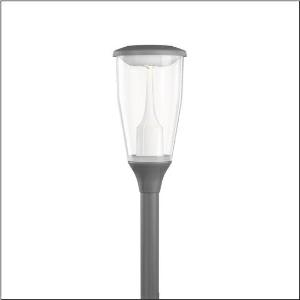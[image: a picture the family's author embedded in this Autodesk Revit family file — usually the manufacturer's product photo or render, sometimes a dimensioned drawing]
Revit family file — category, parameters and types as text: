
# Revit family: dl_11_iq___p1_0a_5xa5565bf14h000022_0962
name_source: partatom
category: Lighting Fixtures
units: mm (PartAtom-declared; Revit-internal decimal feet)

## family parameters
Cut with Voids When Loaded = No
Host = Face
Light Source = No
Part Type = Normal
Room Calculation Point = No
Round Connector Dimension = Use Diameter
Shared = No

## types (1)
- --- (1 x LED, 1530 lm, 12.9 W, 2200K)
    Apparent Load = 13 VA
    CIE Flux Codes = 34 63 91 95 100
    Color Rendering = 70
    Color Temperature = 2200K
    Default Elevation = 1800 mm
    Description = DL 11 iQ, mast luminaire, Module 540 iQ-SR, primary light control with 3 zone facetted reflector, of plastic, silver coated, highly specular, structured, primary optical cover: cover, of PMMA, transparent, light distribution: P1.0a, light emission: direct distribution, primary light characteristic: asymmetric, installation type: post-top, LED, High Power LED, rated luminous flux: 1.560lm, luminous efficacy: 149lm/W, light colour: 722, colour temperature: 2200K, control: Street-Remote, Auto-Match, Temp-Guard, Lumen-Switch, Night-Set, Smart-Wire, Light-Fading, Desk-Remote (wireless, voltage-free reading and setting of iQ features in the workshop via application-optimized NFC function/RFID function), optimised constant luminous flux control (CLO 2.0), mains connection: 220..240V, AC, 50/60Hz, connection cable pre-assembled, cable length: 5,5m, start of lifetime: 13W, end of service life: 13W, reduction: 5W, luminaire housing, upper part, of diecast aluminium, coated, Siteco® metallic grey (DB 702S), spigot size: 60mm (post-top), post-top mast mounting element, of diecast aluminium, coated, Siteco® metallic grey (DB 702S), Module 540 iQ-SR, traffic white (RAL 9016), equipment: standard, protection rating (complete): IP66, insulation class (complete): insulation class II (safety insulation), certification: CE, ENEC, ENEC+, VDE, packaging unit: 1 piece

Light Distribution: P1.0a
    Height = 665 mm
    Lamp = 1 x LED
    Lamp Light Flux = 1530 lm
    Lamp Power = 12.9 W
    Lamp count = 1
    Length = 334 mm
    Luminous efficacy = 119 lm/W
    Manufacturer = Siteco
    ModVariant = No
    Model = 5XA5565BF14H000022
    Number of Poles = 1
    OnlyDefault = Yes
    Power Factor = 1
    Product Name = DL 11 iQ | P1.0a
    Product group = mast luminaire | pylon top
    ProductGroupID = 6100
    Protection Class = Protection class II
    Protection Degree = IP 66
    RLX_Detail_Level = 1
    RLX_Emergency_Light_Flux = 0 lm
    RLX_Emergency_Type = 0
    RLX_Emergency_Type_DB = No
    RlxData = <blob elided: 103685 chars, md5=4187516b>
    Socket = socket
    Standby Power = 0 W
    System Light Flux = 1530 lm
    System Power = 13 W
    Type Comments = factory setting: luminous flux: 100 % | dim-lin: 254 | 516 mA
    Type Image = l_1258354.jpg
    URL = http://relux.com
    VarID = @adj_024311
    Voltage = 0 V
    Weight = 0.00 kg
    Width = 0 mm  [stored 0 ft]

note: [stored X ft] marks values corroborated as IEEE doubles in the binary element streams (Revit-internal decimal feet)

## geometry (parser evidence)
native form markers: Blend x4, Sweep x10
no freeform markers — native parametric forms only
